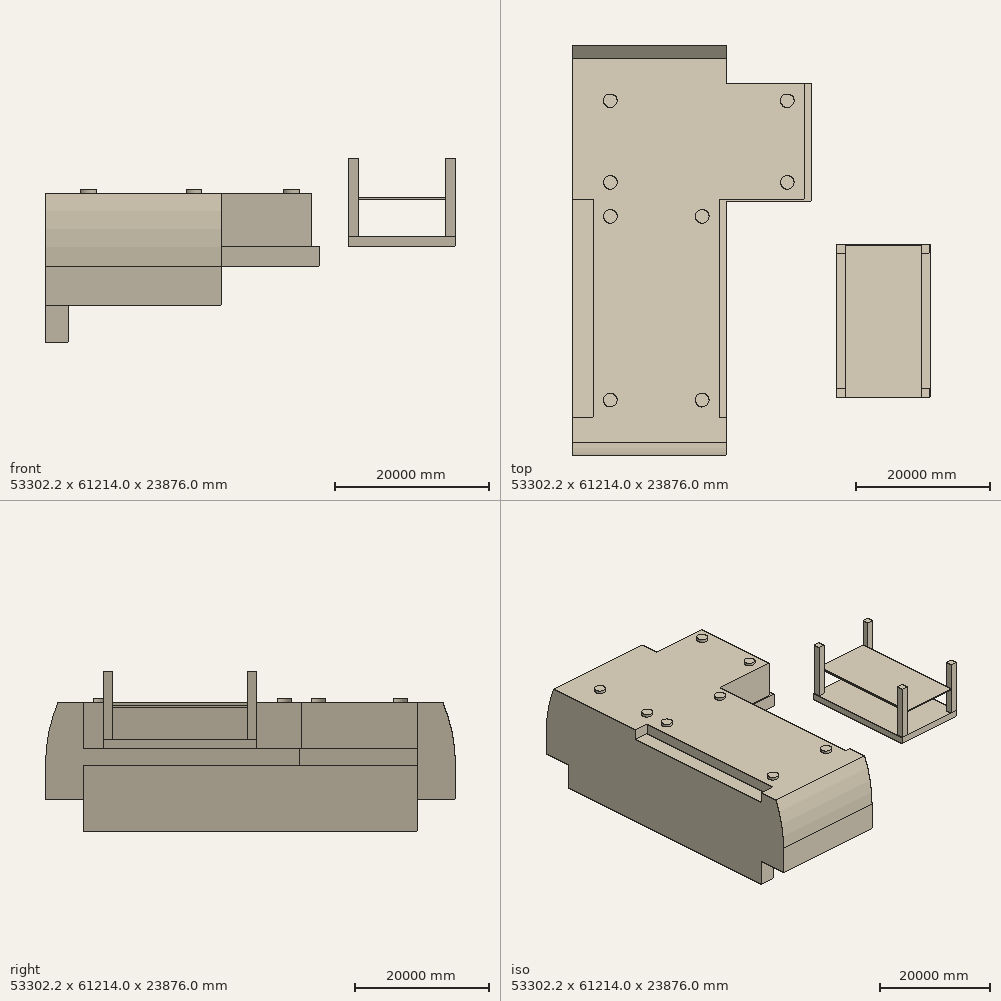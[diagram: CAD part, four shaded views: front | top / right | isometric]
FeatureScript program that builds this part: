
annotation { "Feature Type Name" : "Feature", "Feature Type Description" : "" }
export const myFeature = defineFeature(function(context is Context, id is Id, definition is map)
    precondition{}
    {
        {
            var Q0;
            Q0=qCreatedBy(makeId("Top.planeOp"),FACE);
            var sketch = newSketch(context, id + "F0", { "sketchPlane" : qUnion([Q0])});
            skLineSegment(sketch, "E0.bottom", {"start": v(6985, -11430) * mm, "end": v(-6985, -11430) * mm});
            skLineSegment(sketch, "E0.top", {"start": v(6985, 11430) * mm, "end": v(-6985, 11430) * mm});
            skLineSegment(sketch, "E0.left", {"start": v(6985, -11430) * mm, "end": v(6985, 11430) * mm});
            skLineSegment(sketch, "E0.right", {"start": v(-6985, -11430) * mm, "end": v(-6985, 11430) * mm});
            skPoint(sketch, "E0.middle", {"position": v(0, 0) * mm});
            skSolve(sketch);
        }
        {
            var Q0;
            Q0 = qSketchRegion(id + "F0", true);
            extrude(context, id + "F1", {"entities" : qUnion([Q0]), "depth" : 1270 * mm, "offsetDistance" : 25.4 * mm});
        }
        {
            var Q0;
            Q0=makeQuery(id+"F1.opExtrude","CAP_FACE",FACE,{"disambiguationData":[OSD([sQuery(id+"F0.wireOp",EDGE,"E0.bottom"),sQuery(id+"F0.wireOp",EDGE,"E0.top"),sQuery(id+"F0.wireOp",EDGE,"E0.left"),sQuery(id+"F0.wireOp",EDGE,"E0.right")])],"isStart":false});
            var sketch = newSketch(context, id + "F2", { "sketchPlane" : qUnion([Q0])});
            skLineSegment(sketch, "E1.bottom", {"start": v(-6934.2, 11379.2) * mm, "end": v(-5664.2, 11379.2) * mm});
            skLineSegment(sketch, "E1.top", {"start": v(-6934.2, 10109.2) * mm, "end": v(-5664.2, 10109.2) * mm});
            skLineSegment(sketch, "E1.left", {"start": v(-6934.2, 11379.2) * mm, "end": v(-6934.2, 10109.2) * mm});
            skLineSegment(sketch, "E1.right", {"start": v(-5664.2, 11379.2) * mm, "end": v(-5664.2, 10109.2) * mm});
            skLineSegment(sketch, "E2.bottom", {"start": v(6934.2, 11379.2) * mm, "end": v(5664.2, 11379.2) * mm});
            skLineSegment(sketch, "E2.top", {"start": v(6934.2, 10109.2) * mm, "end": v(5664.2, 10109.2) * mm});
            skLineSegment(sketch, "E2.left", {"start": v(6934.2, 11379.2) * mm, "end": v(6934.2, 10109.2) * mm});
            skLineSegment(sketch, "E2.right", {"start": v(5664.2, 11379.2) * mm, "end": v(5664.2, 10109.2) * mm});
            skLineSegment(sketch, "E3.bottom", {"start": v(-6934.2, -10109.2) * mm, "end": v(-5664.2, -10109.2) * mm});
            skLineSegment(sketch, "E3.top", {"start": v(-6934.2, -11379.2) * mm, "end": v(-5664.2, -11379.2) * mm});
            skLineSegment(sketch, "E3.left", {"start": v(-6934.2, -10109.2) * mm, "end": v(-6934.2, -11379.2) * mm});
            skLineSegment(sketch, "E3.right", {"start": v(-5664.2, -10109.2) * mm, "end": v(-5664.2, -11379.2) * mm});
            skLineSegment(sketch, "E4.bottom", {"start": v(6934.2, -10109.2) * mm, "end": v(5664.2, -10109.2) * mm});
            skLineSegment(sketch, "E4.top", {"start": v(6934.2, -11379.2) * mm, "end": v(5664.2, -11379.2) * mm});
            skLineSegment(sketch, "E4.left", {"start": v(6934.2, -10109.2) * mm, "end": v(6934.2, -11379.2) * mm});
            skLineSegment(sketch, "E4.right", {"start": v(5664.2, -10109.2) * mm, "end": v(5664.2, -11379.2) * mm});
            skSolve(sketch);
        }
        {
            var Q0;
            Q0 = qSketchRegion(id + "F2", true);
            extrude(context, id + "F3", {"entities" : qUnion([Q0]), "operationType" : NewBodyOperationType.ADD, "depth" : 10160 * mm, "offsetDistance" : 25.4 * mm});
        }
        {
            var Q0;
            Q0=makeQuery(id+"F3.opExtrude","CAP_FACE",FACE,{"disambiguationData":[OSD([sQuery(id+"F2.wireOp",EDGE,"E3.bottom"),sQuery(id+"F2.wireOp",EDGE,"E3.top"),sQuery(id+"F2.wireOp",EDGE,"E3.left"),sQuery(id+"F2.wireOp",EDGE,"E3.right")])],"isStart":false});
            cPlane(context, id + "F4", {"entities" : qUnion([Q0]), "cplaneType" : CPlaneType.OFFSET, "offset" : 5080 * mm, "oppositeDirection" : true, "width" : 152.4 * mm, "height" : 152.4 * mm});
        }
        {
            var Q0;
            Q0=qCreatedBy(id+"F4.planeOp",FACE);
            var sketch = newSketch(context, id + "F5", { "sketchPlane" : qUnion([Q0])});
            skLineSegment(sketch, "E5.bottom", {"start": v(-5664.2, 11353.8) * mm, "end": v(5664.2, 11353.8) * mm});
            skLineSegment(sketch, "E5.top", {"start": v(-5664.2, -11353.8) * mm, "end": v(5664.2, -11353.8) * mm});
            skLineSegment(sketch, "E5.left", {"start": v(-5664.2, 11353.8) * mm, "end": v(-5664.2, -11353.8) * mm});
            skLineSegment(sketch, "E5.right", {"start": v(5664.2, 11353.8) * mm, "end": v(5664.2, -11353.8) * mm});
            skSolve(sketch);
        }
        {
            var Q0;
            Q0 = qSketchRegion(id + "F5", true);
            extrude(context, id + "F6", {"entities" : qUnion([Q0]), "operationType" : NewBodyOperationType.ADD, "oppositeDirection" : true, "depth" : 254 * mm, "offsetDistance" : 25.4 * mm});
        }
        {
            var Q0;
            Q0=qCreatedBy(makeId("Top.planeOp"),FACE);
            var sketch = newSketch(context, id + "F7", { "sketchPlane" : qUnion([Q0])});
            skLineSegment(sketch, "E6.bottom", {"start": v(-24473.2, -14357.56) * mm, "end": v(-43269.2, -14357.56) * mm});
            skLineSegment(sketch, "E6.top", {"start": v(-24473.2, 18154.44) * mm, "end": v(-43269.2, 18154.44) * mm});
            skLineSegment(sketch, "E6.left", {"start": v(-24473.2, -14357.56) * mm, "end": v(-24473.2, 18154.44) * mm});
            skLineSegment(sketch, "E6.right", {"start": v(-43269.2, -14357.56) * mm, "end": v(-43269.2, 18154.44) * mm});
            skSolve(sketch);
        }
        {
            var Q0;
            Q0=makeQuery(id+"F7.imprint","IMPRINT",FACE,{"disambiguationData":[TD([[makeQuery(id+"F7.imprint","IMPRINT",EDGE,{"derivedFrom":sQuery(id+"F7.wireOp",EDGE,"E6.bottom")}),-1.0]])]});
            extrude(context, id + "F8", {"entities" : qUnion([Q0]), "depth" : 6858 * mm, "offsetDistance" : 25.4 * mm});
        }
        {
            var Q0;
            Q0=makeQuery(id+"F8.opExtrude","CAP_FACE",FACE,{"disambiguationData":[OSD([sQuery(id+"F7.wireOp",EDGE,"E6.bottom"),sQuery(id+"F7.wireOp",EDGE,"E6.top"),sQuery(id+"F7.wireOp",EDGE,"E6.left"),sQuery(id+"F7.wireOp",EDGE,"E6.right")])],"isStart":true});
            var sketch = newSketch(context, id + "F9", { "sketchPlane" : qUnion([Q0])});
            skLineSegment(sketch, "E7.bottom", {"start": v(-43269.2, -18154.44) * mm, "end": v(-11773.2, -18154.44) * mm});
            skLineSegment(sketch, "E7.top", {"start": v(-43269.2, -35426.44) * mm, "end": v(-11773.2, -35426.44) * mm});
            skLineSegment(sketch, "E7.left", {"start": v(-43269.2, -18154.44) * mm, "end": v(-43269.2, -35426.44) * mm});
            skLineSegment(sketch, "E7.right", {"start": v(-11773.2, -18154.44) * mm, "end": v(-11773.2, -35426.44) * mm});
            skSolve(sketch);
        }
        {
            var Q0;
            Q0 = qSketchRegion(id + "F9", true);
            var Q1;
            Q1=makeQuery(id+"F8.opExtrude","CAP_FACE",FACE,{"disambiguationData":[OSD([sQuery(id+"F7.wireOp",EDGE,"E6.bottom"),sQuery(id+"F7.wireOp",EDGE,"E6.top"),sQuery(id+"F7.wireOp",EDGE,"E6.left"),sQuery(id+"F7.wireOp",EDGE,"E6.right")])],"isStart":false});
            extrude(context, id + "F10", {"entities" : qUnion([Q0]), "operationType" : NewBodyOperationType.ADD, "endBound" : BoundingType.UP_TO_SURFACE, "oppositeDirection" : true, "depth" : 25.4 * mm, "endBoundEntityFace" : qUnion([Q1]), "offsetDistance" : 25.4 * mm});
        }
        {
            var Q0;
            Q0=makeQuery(id+"F8.opExtrude","SWEPT_FACE",FACE,{"disambiguationData":[OSD([sQuery(id+"F7.wireOp",EDGE,"E6.left")])]});
            cPlane(context, id + "F11", {"entities" : qUnion([Q0]), "cplaneType" : CPlaneType.OFFSET, "offset" : 1016 * mm, "width" : 152.4 * mm, "height" : 152.4 * mm});
        }
        {
            var Q0;
            Q0=qCreatedBy(id+"F11.planeOp",FACE);
            var sketch = newSketch(context, id + "F12", { "sketchPlane" : qUnion([Q0])});
            skLineSegment(sketch, "E8", {"start": v(-14357.56, 6858) * mm, "end": v(-18167.56, 6858) * mm});
            skLineSegment(sketch, "E9", {"start": v(-14357.56, 6858) * mm, "end": v(-14357.56, -7620) * mm});
            skLineSegment(sketch, "E10", {"start": v(-14357.56, -7620) * mm, "end": v(-20072.56, -7620) * mm});
            skLineSegment(sketch, "E11", {"start": v(-20072.56, -7620) * mm, "end": v(-20072.56, -2540) * mm});
            skArc(sketch, "E12", {"start": v(-20072.56, -2540) * mm, "mid": v(-19591.52, 2254.57) * mm, "end": v(-18167.56, 6858) * mm});
            skLineSegment(sketch, "E13", {"start": v(39236.44, 6858) * mm, "end": v(35426.44, 6858) * mm});
            skLineSegment(sketch, "E14", {"start": v(35426.44, 6858) * mm, "end": v(35426.44, -7620) * mm});
            skLineSegment(sketch, "E15", {"start": v(35426.44, -7620) * mm, "end": v(41141.44, -7620) * mm});
            skLineSegment(sketch, "E16", {"start": v(41141.44, -7620) * mm, "end": v(41141.44, -2540) * mm});
            skArc(sketch, "E17", {"start": v(41141.44, -2540) * mm, "mid": v(40660.4, 2254.57) * mm, "end": v(39236.44, 6858) * mm});
            skSolve(sketch);
        }
        {
            var Q0;
            Q0 = qSketchRegion(id + "F12", true);
            extrude(context, id + "F13", {"entities" : qUnion([Q0]), "operationType" : NewBodyOperationType.ADD, "oppositeDirection" : true, "depth" : 22860 * mm, "offsetDistance" : 25.4 * mm});
        }
        {
            var Q0;
            {var subQ0=sQuery(id+"F7.wireOp",EDGE,"E6.right");var subQ1=sQuery(id+"F7.wireOp",EDGE,"E6.left");var subQ2=sQuery(id+"F7.wireOp",EDGE,"E6.top");var subQ3=sQuery(id+"F7.wireOp",EDGE,"E6.bottom");Q0=makeQuery(id+"F13.boolean.opBoolean","MERGE",FACE,{"derivedFrom":[makeQuery(id+"F10.boolean.opBoolean","MERGE",FACE,{"derivedFrom":[makeQuery(id+"F8.opExtrude","CAP_FACE",FACE,{"disambiguationData":[OSD([subQ3,subQ2,subQ1,subQ0])],"isStart":false}),makeQuery(id+"F10.opExtrude","CAP_FACE",FACE,{"disambiguationData":[OSD([subQ3,subQ2,subQ1,subQ0])],"isStart":false})]}),makeQuery(id+"F13.opExtrude","SWEPT_FACE",FACE,{"disambiguationData":[OSD([sQuery(id+"F12.wireOp",EDGE,"E8")])]}),makeQuery(id+"F13.opExtrude","SWEPT_FACE",FACE,{"disambiguationData":[OSD([sQuery(id+"F12.wireOp",EDGE,"E13")])]})]});}
            var sketch = newSketch(context, id + "F14", { "sketchPlane" : qUnion([Q0])});
            skCircle(sketch, "E18", {"center": v(-14313.2, 32886.44) * mm, "radius": 1016 * mm});
            skCircle(sketch, "E19", {"center": v(-14313.2, 20694.44) * mm, "radius": 1016 * mm});
            skCircle(sketch, "E20", {"center": v(-40729.2, 20694.44) * mm, "radius": 1016 * mm});
            skCircle(sketch, "E21", {"center": v(-40729.2, 32886.44) * mm, "radius": 1016 * mm});
            skCircle(sketch, "E22", {"center": v(-40729.2, 15614.44) * mm, "radius": 1016 * mm});
            skCircle(sketch, "E23", {"center": v(-27013.2, 15614.44) * mm, "radius": 1016 * mm});
            skCircle(sketch, "E24", {"center": v(-40729.2, -11817.56) * mm, "radius": 1016 * mm});
            skCircle(sketch, "E25", {"center": v(-27013.2, -11817.56) * mm, "radius": 1016 * mm});
            skLineSegment(sketch, "E26.bottom", {"start": v(-40729.2, 32886.44) * mm, "end": v(-14313.2, 32886.44) * mm, "construction": true});
            skLineSegment(sketch, "E26.top", {"start": v(-40729.2, 20694.44) * mm, "end": v(-14313.2, 20694.44) * mm, "construction": true});
            skLineSegment(sketch, "E26.left", {"start": v(-40729.2, 32886.44) * mm, "end": v(-40729.2, 20694.44) * mm, "construction": true});
            skLineSegment(sketch, "E26.right", {"start": v(-14313.2, 32886.44) * mm, "end": v(-14313.2, 20694.44) * mm, "construction": true});
            skLineSegment(sketch, "E27.bottom", {"start": v(-40729.2, 15614.44) * mm, "end": v(-27013.2, 15614.44) * mm, "construction": true});
            skLineSegment(sketch, "E27.top", {"start": v(-40729.2, -11817.56) * mm, "end": v(-27013.2, -11817.56) * mm, "construction": true});
            skLineSegment(sketch, "E27.left", {"start": v(-40729.2, 15614.44) * mm, "end": v(-40729.2, -11817.56) * mm, "construction": true});
            skLineSegment(sketch, "E27.right", {"start": v(-27013.2, 15614.44) * mm, "end": v(-27013.2, -11817.56) * mm, "construction": true});
            skSolve(sketch);
        }
        {
            var Q0;
            Q0 = qSketchRegion(id + "F14", true);
            extrude(context, id + "F15", {"entities" : qUnion([Q0]), "operationType" : NewBodyOperationType.ADD, "depth" : 508 * mm, "offsetDistance" : 25.4 * mm});
        }
        {
            var Q0;
            Q0=makeQuery(id+"F15.opExtrude","CAP_FACE",FACE,{"disambiguationData":[OSD([sQuery(id+"F14.wireOp",EDGE,"E24")])],"isStart":false});
            cPlane(context, id + "F16", {"entities" : qUnion([Q0]), "cplaneType" : CPlaneType.OFFSET, "offset" : 19812 * mm, "oppositeDirection" : true, "width" : 152.4 * mm, "height" : 152.4 * mm});
        }
        {
            var Q0;
            Q0=qCreatedBy(id+"F16.planeOp",FACE);
            var sketch = newSketch(context, id + "F17", { "sketchPlane" : qUnion([Q0])});
            skLineSegment(sketch, "E28.bottom", {"start": v(-46317.2, 35426.44) * mm, "end": v(-43269.2, 35426.44) * mm});
            skLineSegment(sketch, "E28.top", {"start": v(-46317.2, -14357.56) * mm, "end": v(-43269.2, -14357.56) * mm});
            skLineSegment(sketch, "E28.left", {"start": v(-46317.2, 35426.44) * mm, "end": v(-46317.2, -14357.56) * mm});
            skLineSegment(sketch, "E28.right", {"start": v(-43269.2, 35426.44) * mm, "end": v(-43269.2, -14357.56) * mm});
            skSolve(sketch);
        }
        {
            var Q0;
            Q0 = qSketchRegion(id + "F17", true);
            extrude(context, id + "F18", {"entities" : qUnion([Q0]), "operationType" : NewBodyOperationType.ADD, "depth" : 17272 * mm, "offsetDistance" : 25.4 * mm});
        }
        {
            var Q0;
            {var subQ0=sQuery(id+"F7.wireOp",EDGE,"E6.right");var subQ1=sQuery(id+"F7.wireOp",EDGE,"E6.left");var subQ2=sQuery(id+"F7.wireOp",EDGE,"E6.top");var subQ3=sQuery(id+"F7.wireOp",EDGE,"E6.bottom");Q0=makeQuery(id+"F13.boolean.opBoolean","MERGE",FACE,{"derivedFrom":[makeQuery(id+"F10.boolean.opBoolean","MERGE",FACE,{"derivedFrom":[makeQuery(id+"F8.opExtrude","CAP_FACE",FACE,{"disambiguationData":[OSD([subQ3,subQ2,subQ1,subQ0])],"isStart":false}),makeQuery(id+"F10.opExtrude","CAP_FACE",FACE,{"disambiguationData":[OSD([subQ3,subQ2,subQ1,subQ0])],"isStart":false})]}),makeQuery(id+"F13.opExtrude","SWEPT_FACE",FACE,{"disambiguationData":[OSD([sQuery(id+"F12.wireOp",EDGE,"E8")])]}),makeQuery(id+"F13.opExtrude","SWEPT_FACE",FACE,{"disambiguationData":[OSD([sQuery(id+"F12.wireOp",EDGE,"E13")])]})]});}
            var sketch = newSketch(context, id + "F19", { "sketchPlane" : qUnion([Q0])});
            skLineSegment(sketch, "E29.bottom", {"start": v(-46317.2, 18154.44) * mm, "end": v(-42058.89, 18154.44) * mm});
            skLineSegment(sketch, "E29.top", {"start": v(-46317.2, 37364.8) * mm, "end": v(-42058.89, 37364.8) * mm});
            skLineSegment(sketch, "E29.left", {"start": v(-46317.2, 18154.44) * mm, "end": v(-46317.2, 37364.8) * mm});
            skLineSegment(sketch, "E29.right", {"start": v(-42058.89, 18154.44) * mm, "end": v(-42058.89, 37364.8) * mm});
            skSolve(sketch);
        }
        {
            var Q0;
            Q0 = qSketchRegion(id + "F19", true);
            extrude(context, id + "F20", {"entities" : qUnion([Q0]), "operationType" : NewBodyOperationType.ADD, "oppositeDirection" : true, "depth" : 3810 * mm, "offsetDistance" : 25.4 * mm});
        }
        {
            var Q0;
            Q0=makeQuery(id+"F10.boolean.opBoolean","MERGE",FACE,{"derivedFrom":[makeQuery(id+"F8.opExtrude","CAP_FACE",FACE,{"disambiguationData":[OSD([sQuery(id+"F7.wireOp",EDGE,"E6.bottom"),sQuery(id+"F7.wireOp",EDGE,"E6.top"),sQuery(id+"F7.wireOp",EDGE,"E6.left"),sQuery(id+"F7.wireOp",EDGE,"E6.right")])],"isStart":true}),makeQuery(id+"F10.opExtrude","CAP_FACE",FACE,{"disambiguationData":[OSD([sQuery(id+"F9.wireOp",EDGE,"E7.bottom"),sQuery(id+"F9.wireOp",EDGE,"E7.top"),sQuery(id+"F9.wireOp",EDGE,"E7.left"),sQuery(id+"F9.wireOp",EDGE,"E7.right")])],"isStart":true})]});
            var sketch = newSketch(context, id + "F21", { "sketchPlane" : qUnion([Q0])});
            skLineSegment(sketch, "E30", {"start": v(-43269.2, 14357.56) * mm, "end": v(-23457.2, 14357.56) * mm});
            skLineSegment(sketch, "E31", {"start": v(-23457.2, 14357.56) * mm, "end": v(-23457.2, -17900.44) * mm});
            skLineSegment(sketch, "E32", {"start": v(-23457.2, -17900.44) * mm, "end": v(-10757.2, -17900.44) * mm});
            skLineSegment(sketch, "E33", {"start": v(-10757.2, -17900.44) * mm, "end": v(-10757.2, -35426.44) * mm});
            skLineSegment(sketch, "E34", {"start": v(-10757.2, -35426.44) * mm, "end": v(-43269.2, -35426.44) * mm});
            skLineSegment(sketch, "E35", {"start": v(-43269.2, -35426.44) * mm, "end": v(-43269.2, 14357.56) * mm});
            skSolve(sketch);
        }
        {
            var Q0;
            Q0 = qSketchRegion(id + "F21", true);
            extrude(context, id + "F22", {"entities" : qUnion([Q0]), "operationType" : NewBodyOperationType.ADD, "depth" : 2540 * mm, "offsetDistance" : 25.4 * mm});
        }
    });
